# Revit family: IS_Contour21_K7927_BIM_DE
name_source: partatom
category: Plumbing Fixtures
revit_build: Autodesk Revit MEP 2016 (Build: 20161004_0715(x64)
units: mm (PartAtom-declared; Revit-internal decimal feet)

## family parameters
Always vertical = No
Cut with Voids When Loaded = No
OmniClass Number = 23.45.05.21.11.11
OmniClass Title = Water Operated Water Closets
Part Type = Normal
Room Calculation Point = No
Round Connector Dimension = Use Diameter
Shared = No
Work Plane-Based = No

## types (1)
- K792701 - CONTOUR21 seat & cover with hinges
    Accessories = www.idealstandard.de\ersatzteile
    AssetType = Fixed
    BIMObjectName = ISI_IdealStandard_WcSeatsAndCovers_Contour21_K792701
    BIMobject category = Toilet Seats
    BOSUseNativeGeometries = 1
    BarCode = 4015413039338
    Brand = Ideal Standard
    Brand url = http://www.idealstandard.de
    Color = White
    ConnectionType = Plumbing
    Cost = 0 $
    CurrencyUnit = €
    CurrentRevision = 1
    Date of publishing = 20/12/2017
    Description = IS WC-Sitz CONTOUR 21, mit Stangenscharnier, Weiß
    DurationUnit = Year
    EAN code = https://4015413039338
    Edition number = 1
    ExpectedLife = 25
    Features = IS WC-Sitz CONTOUR 21, mit Stangenscharnier, Weiß
    Finish = White
    IFC Classification = Sanitary Terminal
    IfcExportAs = IfcSanitaryTerminalType
    Installation instructions = http://www.idealstandard.de
    InstallationInstructions = www.idealstandard.de\produkte
    MainColor = White
    MaintenanceInformation = www.idealstandard.de\produkte
    Manufacturer name = Ideal Standard
    ManufacturerURL = http://www.idealstandard.de
    Material = Duroplast
    Model = K792701
    ModelNumber = K792701
    ModelReference = IS WC-Sitz CONTOUR 21, mit Stangenscharnier, Weiß
    NBS Reference Code = 35-93-95
    NBS Reference Description = Wc Seats And Covers
    Name = WcSeatsAndCovers_Contour21_K792701
    NettWeight = 1.9 Kg
    Nominal height = 0
    Nominal width = 0
    NominalDepth = 439 mm  [stored 1.44029 ft]
    NominalHeight = 53 mm
    NominalLength = 439 mm  [stored 1.44029 ft]
    NominalWidth = 366 mm
    OmniClass Code = 23-31 19 00
    OmniClass Description = Toilets
    OutletConnectionSize = 0 mm  [stored 0 ft]
    Product Guid = eb6b8e2d-0be6-457e-9388-dd3ac1675048
    Product SKU = K7927
    Product data url = https://bimobject.com
    Product family = Sanitary
    Product group = Seat & Cover
    Product name = CONTOUR21 seat & cover with hinges
    Product url = http://www.idealstandard.de
    ProductInformation = www.idealstandard.de/produkte
    QR code = http://bimobject.com
    Shape = Sculptured
    Size = 53 x 439 x 366mm
    Space = Internal
    SpareParts = www.idealstandard.de/ersatzteile
    SpilloverLevel = 0 mm  [stored 0 ft]
    Technical description = http://www.idealstandard.de
    URL = http://www.idealstandard.de
    Uniclass 1.4 Code = L7216
    Uniclass 1.4 Description = Toilets
    Uniclass 2.0 Code = PR-35-93-95
    Uniclass 2.0 Description = Wc Seats And Covers
    Uniclass 2015 Code = Pr_40_20_93_95
    Uniclass 2015 Name = WC seats and covers
    Uniclass2015Code = Pr_40_20_93_95
    Uniclass2015Title = WC seats and covers
    Uniclass2015Version = Products v1.1
    Version = 1
    VolumeUnits = Litres
    Weight Net (Kg) = 1.9

note: [stored X ft] marks values corroborated as IEEE doubles in the binary element streams (Revit-internal decimal feet)

## geometry (parser evidence)
native form markers: Blend x4, Sweep x1
no freeform markers — native parametric forms only
